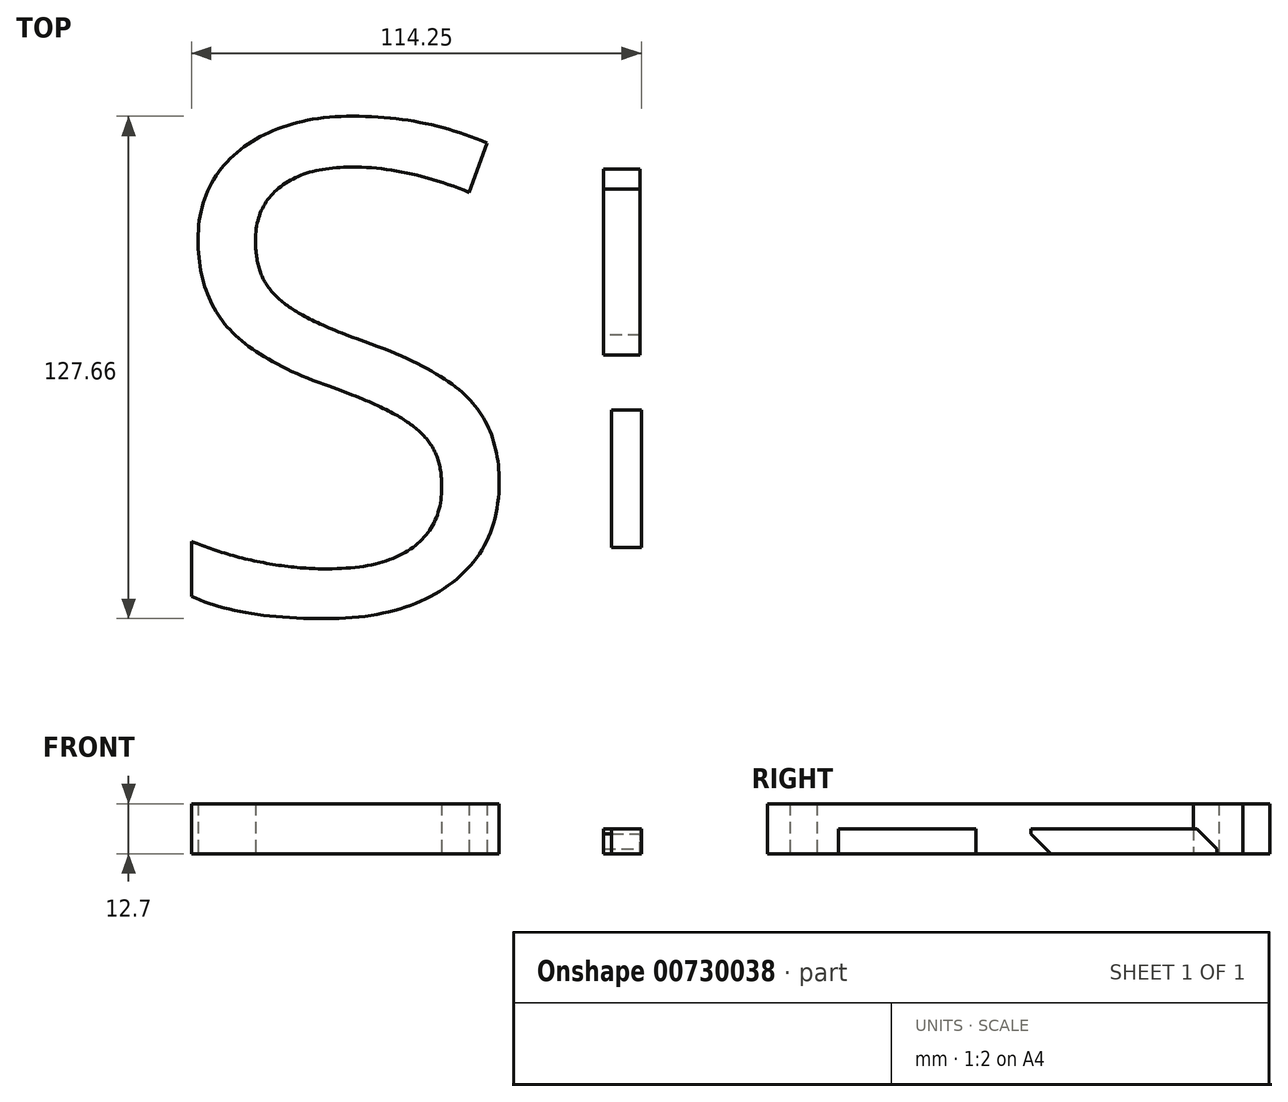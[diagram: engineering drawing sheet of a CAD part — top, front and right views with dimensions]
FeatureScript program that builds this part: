
annotation { "Feature Type Name" : "Feature", "Feature Type Description" : "" }
export const myFeature = defineFeature(function(context is Context, id is Id, definition is map)
    precondition{}
    {
        {
            var Q0;
            Q0=qCreatedBy(makeId("Top.planeOp"),FACE);
            var sketch = newSketch(context, id + "F0", { "sketchPlane" : qUnion([Q0])});
            skText(sketch, "E0", { "text": "S", "fontName": "OpenSans-Regular.ttf"});
            const initialGuessF0  = {"E0": [-0.05701, -0.06532, 1, 0, 0.12524]};
            skSetInitialGuess(sketch, initialGuessF0);
            skSolve(sketch);
        }
        {
            var Q0;
            Q0=qCreatedBy(makeId("Top.planeOp"),FACE);
            var sketch = newSketch(context, id + "F1", { "sketchPlane" : qUnion([Q0])});
            skLineSegment(sketch, "E1.bottom", {"start": v(56.63, 0) * mm, "end": v(65.9, 0) * mm});
            skLineSegment(sketch, "E1.top", {"start": v(56.63, 47.16) * mm, "end": v(65.9, 47.16) * mm});
            skLineSegment(sketch, "E1.left", {"start": v(56.63, 0) * mm, "end": v(56.63, 47.16) * mm});
            skLineSegment(sketch, "E1.right", {"start": v(65.9, 0) * mm, "end": v(65.9, 47.16) * mm});
            skPoint(sketch, "E1.middle", {"position": v(61.27, 23.58) * mm});
            skSolve(sketch);
        }
        {
            var Q0;
            Q0 = qSketchRegion(id + "F1", true);
            extrude(context, id + "F2", {"entities" : qUnion([Q0]), "depth" : 6.35 * mm, "offsetDistance" : 25.4 * mm});
        }
        {
            var Q0;
            Q0=makeQuery(id+"F2.opExtrude","CAP_EDGE",EDGE,{"disambiguationData":[OSD([sQuery(id+"F1.wireOp",EDGE,"E1.top")])],"isStart":false});
            chamfer(context, id + "F3", {"entities" : qUnion([Q0]), "width" : 5.08 * mm, "tangentPropagation" : true});
        }
        {
            var Q0;
            Q0=makeQuery(id+"F2.opExtrude","CAP_EDGE",EDGE,{"disambiguationData":[OSD([sQuery(id+"F1.wireOp",EDGE,"E1.bottom")])],"isStart":true});
            chamfer(context, id + "F4", {"entities" : qUnion([Q0]), "width" : 5.08 * mm, "tangentPropagation" : true});
        }
        {
            var Q0;
            Q0 = qSketchRegion(id + "F0", true);
            extrude(context, id + "F5", {"entities" : qUnion([Q0]), "depth" : 12.7 * mm, "offsetDistance" : 25.4 * mm});
        }
        {
            var Q0;
            Q0=qCreatedBy(makeId("Top.planeOp"),FACE);
            var sketch = newSketch(context, id + "F6", { "sketchPlane" : qUnion([Q0])});
            skLineSegment(sketch, "E2.bottom", {"start": v(58.65, -48.97) * mm, "end": v(66.24, -48.97) * mm});
            skLineSegment(sketch, "E2.top", {"start": v(58.65, -14.05) * mm, "end": v(66.24, -14.05) * mm});
            skLineSegment(sketch, "E2.left", {"start": v(58.65, -48.97) * mm, "end": v(58.65, -14.05) * mm});
            skLineSegment(sketch, "E2.right", {"start": v(66.24, -48.97) * mm, "end": v(66.24, -14.05) * mm});
            skPoint(sketch, "E2.middle", {"position": v(62.44, -31.5) * mm});
            skSolve(sketch);
        }
        {
            var Q0;
            Q0 = qSketchRegion(id + "F6", true);
            extrude(context, id + "F7", {"entities" : qUnion([Q0]), "depth" : 6.35 * mm, "offsetDistance" : 25.4 * mm});
        }
    });
